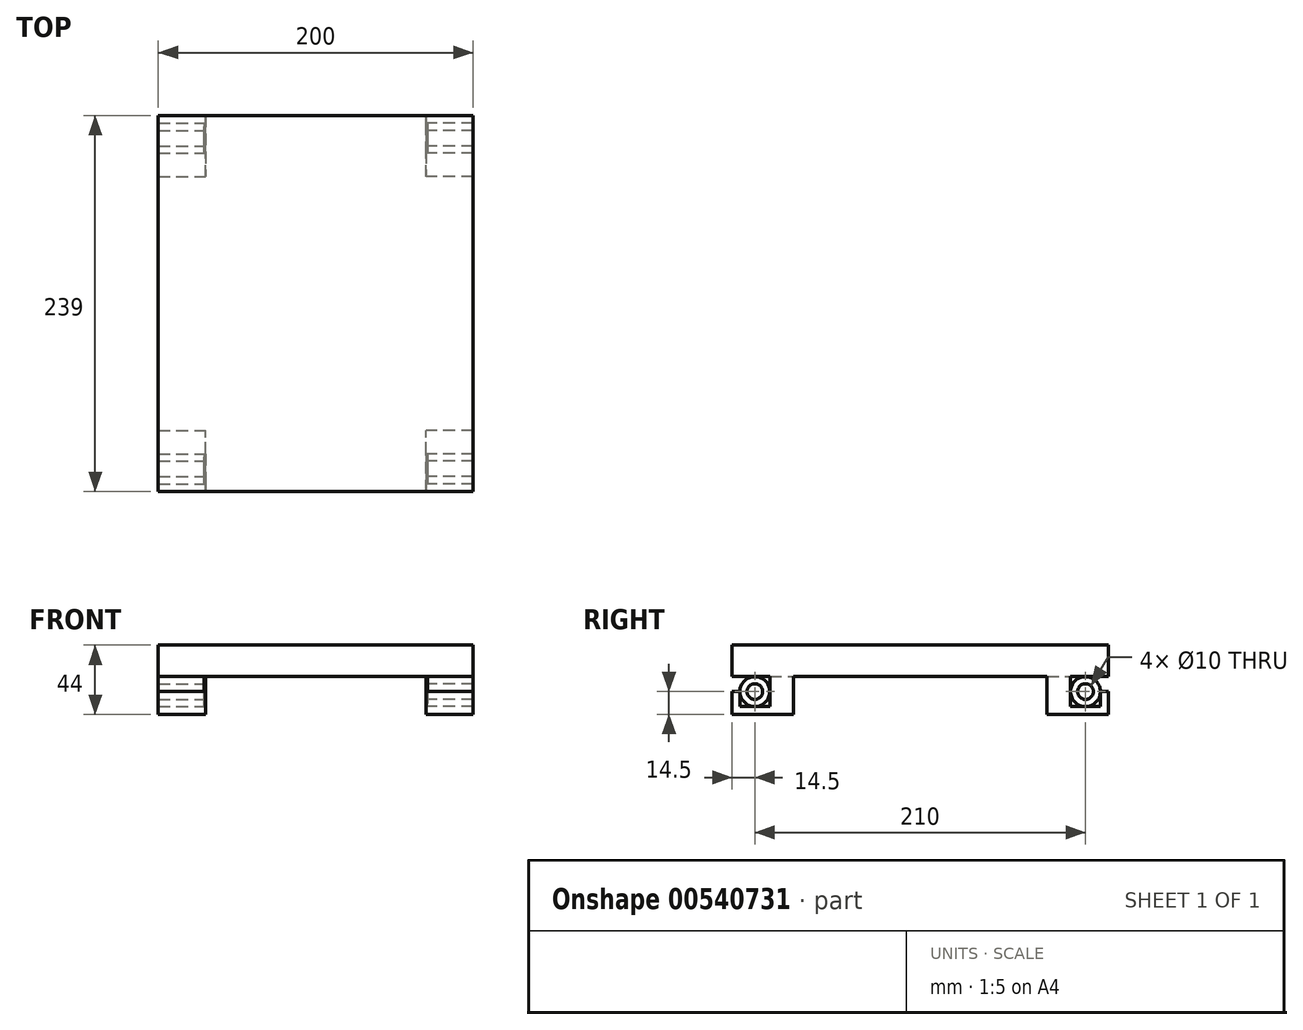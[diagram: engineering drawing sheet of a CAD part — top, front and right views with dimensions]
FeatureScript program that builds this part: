
annotation { "Feature Type Name" : "Feature", "Feature Type Description" : "" }
export const myFeature = defineFeature(function(context is Context, id is Id, definition is map)
    precondition{}
    {
        {
            var Q0;
            Q0=qCreatedBy(makeId("Right.planeOp"),FACE);
            var sketch = newSketch(context, id + "F0", { "sketchPlane" : qUnion([Q0])});
            skLineSegment(sketch, "E0.bottom", {"start": v(-119.5, 0) * mm, "end": v(119.5, 0) * mm});
            skLineSegment(sketch, "E0.top", {"start": v(-119.5, -20) * mm, "end": v(119.5, -20) * mm});
            skLineSegment(sketch, "E0.left", {"start": v(-119.5, 0) * mm, "end": v(-119.5, -20) * mm});
            skLineSegment(sketch, "E0.right", {"start": v(119.5, 0) * mm, "end": v(119.5, -20) * mm});
            skCircle(sketch, "E1", {"center": v(-105, -29.5) * mm, "radius": 9.5 * mm});
            skLineSegment(sketch, "E2", {"start": v(-105, -29.5) * mm, "end": v(105, -29.5) * mm, "construction": true});
            skCircle(sketch, "E3", {"center": v(105, -29.5) * mm, "radius": 9.5 * mm});
            skCircle(sketch, "E4", {"center": v(-105, -29.5) * mm, "radius": 5 * mm});
            skCircle(sketch, "E5", {"center": v(105, -29.5) * mm, "radius": 5 * mm});
            skPoint(sketch, "E6", {"position": v(0, 0) * mm});
            skLineSegment(sketch, "E7", {"start": v(-114.5, -29.5) * mm, "end": v(-119.5, -29.5) * mm});
            skLineSegment(sketch, "E8", {"start": v(-119.5, -29.5) * mm, "end": v(-119.5, -44) * mm});
            skLineSegment(sketch, "E9", {"start": v(-119.5, -44) * mm, "end": v(-80.5, -44) * mm});
            skLineSegment(sketch, "E10", {"start": v(-80.5, -44) * mm, "end": v(-80.5, -20) * mm});
            skLineSegment(sketch, "E11", {"start": v(-95.5, -20) * mm, "end": v(-95.5, -39) * mm});
            skLineSegment(sketch, "E12", {"start": v(-95.5, -39) * mm, "end": v(-114.5, -39) * mm});
            skLineSegment(sketch, "E13", {"start": v(-114.5, -39) * mm, "end": v(-114.5, -29.5) * mm});
            skPoint(sketch, "E14", {"position": v(0, -29.5) * mm});
            skLineSegment(sketch, "E15", {"start": v(0, 0) * mm, "end": v(0, -70.67) * mm, "construction": true});
            skLineSegment(sketch, "E16.MirrorCS", {"start": v(80.5, -44) * mm, "end": v(80.5, -20) * mm});
            skLineSegment(sketch, "E17.MirrorCS", {"start": v(95.5, -20) * mm, "end": v(95.5, -39) * mm});
            skLineSegment(sketch, "E18.MirrorCS", {"start": v(95.5, -39) * mm, "end": v(114.5, -39) * mm});
            skLineSegment(sketch, "E19.MirrorCS", {"start": v(119.5, -44) * mm, "end": v(80.5, -44) * mm});
            skLineSegment(sketch, "E20.MirrorCS", {"start": v(114.5, -39) * mm, "end": v(114.5, -29.5) * mm});
            skLineSegment(sketch, "E21.MirrorCS", {"start": v(114.5, -29.5) * mm, "end": v(119.5, -29.5) * mm});
            skLineSegment(sketch, "E22.MirrorCS", {"start": v(119.5, -29.5) * mm, "end": v(119.5, -44) * mm});
            skSolve(sketch);
        }
        {
            var Q0;
            Q0=makeQuery(id+"F0.imprint","IMPRINT",FACE,{"disambiguationData":[TD([[makeQuery(id+"F0.imprint","IMPRINT",EDGE,{"derivedFrom":sQuery(id+"F0.wireOp",EDGE,"E0.bottom")}),-1.0]])]});
            extrude(context, id + "F1", {"entities" : qUnion([Q0]), "endBound" : BoundingType.SYMMETRIC, "depth" : 200 * mm, "offsetDistance" : 25 * mm});
        }
        {
            var Q0;
            Q0=makeQuery(id+"F0.imprint","IMPRINT",FACE,{"disambiguationData":[TD([[makeQuery(id+"F0.imprint","IMPRINT",EDGE,{"derivedFrom":sQuery(id+"F0.wireOp",EDGE,"E4")}),-1.0]])]});
            var Q1;
            Q1=makeQuery(id+"F0.imprint","IMPRINT",FACE,{"disambiguationData":[TD([[makeQuery(id+"F0.imprint","IMPRINT",EDGE,{"derivedFrom":sQuery(id+"F0.wireOp",EDGE,"E5")}),-1.0]])]});
            var Q2;
            Q2=makeQuery(id+"F1.opExtrude","CAP_FACE",FACE,{"disambiguationData":[OSD([sQuery(id+"F0.wireOp",EDGE,"E0.bottom"),sQuery(id+"F0.wireOp",EDGE,"E0.top"),sQuery(id+"F0.wireOp",EDGE,"E0.left"),sQuery(id+"F0.wireOp",EDGE,"E0.right")])],"isStart":false});
            var Q3;
            Q3=makeQuery(id+"F1.opExtrude","CAP_FACE",FACE,{"disambiguationData":[OSD([sQuery(id+"F0.wireOp",EDGE,"E0.bottom"),sQuery(id+"F0.wireOp",EDGE,"E0.top"),sQuery(id+"F0.wireOp",EDGE,"E0.left"),sQuery(id+"F0.wireOp",EDGE,"E0.right")])],"isStart":false});
            extrude(context, id + "F2", {"entities" : qUnion([Q0, Q1]), "operationType" : NewBodyOperationType.ADD, "endBound" : BoundingType.UP_TO_SURFACE, "depth" : 25 * mm, "endBoundEntityFace" : qUnion([Q2]), "offsetDistance" : 25 * mm, "hasSecondDirection" : true, "secondDirectionBound" : SecondDirectionBoundingType.UP_TO_SURFACE, "secondDirectionOppositeDirection" : false, "secondDirectionDepth" : 25 * mm, "secondDirectionBoundEntityFace" : qUnion([Q3]), "hasSecondDirectionOffset" : true, "secondDirectionOffsetDistance" : 29 * mm});
        }
        {
            var Q0;
            Q0=makeQuery(id+"F0.imprint","IMPRINT",FACE,{"disambiguationData":[TD([[makeQuery(id+"F0.imprint","IMPRINT",EDGE,{"derivedFrom":sQuery(id+"F0.wireOp",EDGE,"E7")}),1.0]])]});
            var Q1;
            {var subQ5=sQuery(id+"F0.wireOp",EDGE,"E16.MirrorCS");Q1=makeQuery(id+"F0.imprint","IMPRINT",FACE,{"disambiguationData":[TD([[makeQuery(id+"F0.imprint","IMPRINT",EDGE,{"derivedFrom":subQ5}),-1.0]])]});}
            var Q2;
            Q2=makeQuery(id+"F1.opExtrude","CAP_FACE",FACE,{"disambiguationData":[OSD([sQuery(id+"F0.wireOp",EDGE,"E0.bottom"),sQuery(id+"F0.wireOp",EDGE,"E0.top"),sQuery(id+"F0.wireOp",EDGE,"E0.left"),sQuery(id+"F0.wireOp",EDGE,"E0.right")])],"isStart":false});
            var Q3;
            Q3=makeQuery(id+"F1.opExtrude","CAP_FACE",FACE,{"disambiguationData":[OSD([sQuery(id+"F0.wireOp",EDGE,"E0.bottom"),sQuery(id+"F0.wireOp",EDGE,"E0.top"),sQuery(id+"F0.wireOp",EDGE,"E0.left"),sQuery(id+"F0.wireOp",EDGE,"E0.right")])],"isStart":false});
            extrude(context, id + "F3", {"entities" : qUnion([Q0, Q1]), "endBound" : BoundingType.UP_TO_SURFACE, "depth" : 25 * mm, "endBoundEntityFace" : qUnion([Q2]), "offsetDistance" : 25 * mm, "hasSecondDirection" : true, "secondDirectionBound" : SecondDirectionBoundingType.UP_TO_SURFACE, "secondDirectionOppositeDirection" : false, "secondDirectionDepth" : 25 * mm, "secondDirectionBoundEntityFace" : qUnion([Q3]), "hasSecondDirectionOffset" : true, "secondDirectionOffsetDistance" : 30 * mm});
        }
        {
            var Q0;
            Q0=makeQuery(id+"F3.opExtrude","SWEPT_BODY",BODY,{"disambiguationData":[OSD([sQuery(id+"F0.wireOp",EDGE,"E0.top"),sQuery(id+"F0.wireOp",EDGE,"E7"),sQuery(id+"F0.wireOp",EDGE,"E8"),sQuery(id+"F0.wireOp",EDGE,"E9"),sQuery(id+"F0.wireOp",EDGE,"E10"),sQuery(id+"F0.wireOp",EDGE,"E11"),sQuery(id+"F0.wireOp",EDGE,"E12"),sQuery(id+"F0.wireOp",EDGE,"E13")])]});
            var Q1;
            Q1=makeQuery(id+"F2.opExtrude","SWEPT_BODY",BODY,{"disambiguationData":[OSD([sQuery(id+"F0.wireOp",EDGE,"E1"),sQuery(id+"F0.wireOp",EDGE,"E4")])]});
            var Q2;
            Q2=makeQuery(id+"F3.opExtrude","SWEPT_BODY",BODY,{"disambiguationData":[OSD([sQuery(id+"F0.wireOp",EDGE,"E0.top"),sQuery(id+"F0.wireOp",EDGE,"E16.MirrorCS"),sQuery(id+"F0.wireOp",EDGE,"E17.MirrorCS"),sQuery(id+"F0.wireOp",EDGE,"E18.MirrorCS"),sQuery(id+"F0.wireOp",EDGE,"E19.MirrorCS"),sQuery(id+"F0.wireOp",EDGE,"E20.MirrorCS"),sQuery(id+"F0.wireOp",EDGE,"E21.MirrorCS"),sQuery(id+"F0.wireOp",EDGE,"E22.MirrorCS")])]});
            var Q3;
            Q3=makeQuery(id+"F2.opExtrude","SWEPT_BODY",BODY,{"disambiguationData":[OSD([sQuery(id+"F0.wireOp",EDGE,"E3"),sQuery(id+"F0.wireOp",EDGE,"E5")])]});
            var Q4;
            Q4=qCreatedBy(makeId("Right.planeOp"),FACE);
            mirror(context, id + "F4", {"operationType" : NewBodyOperationType.ADD, "entities" : qUnion([Q0, Q1, Q2, Q3]), "mirrorPlane" : qUnion([Q4])});
        }
    });
